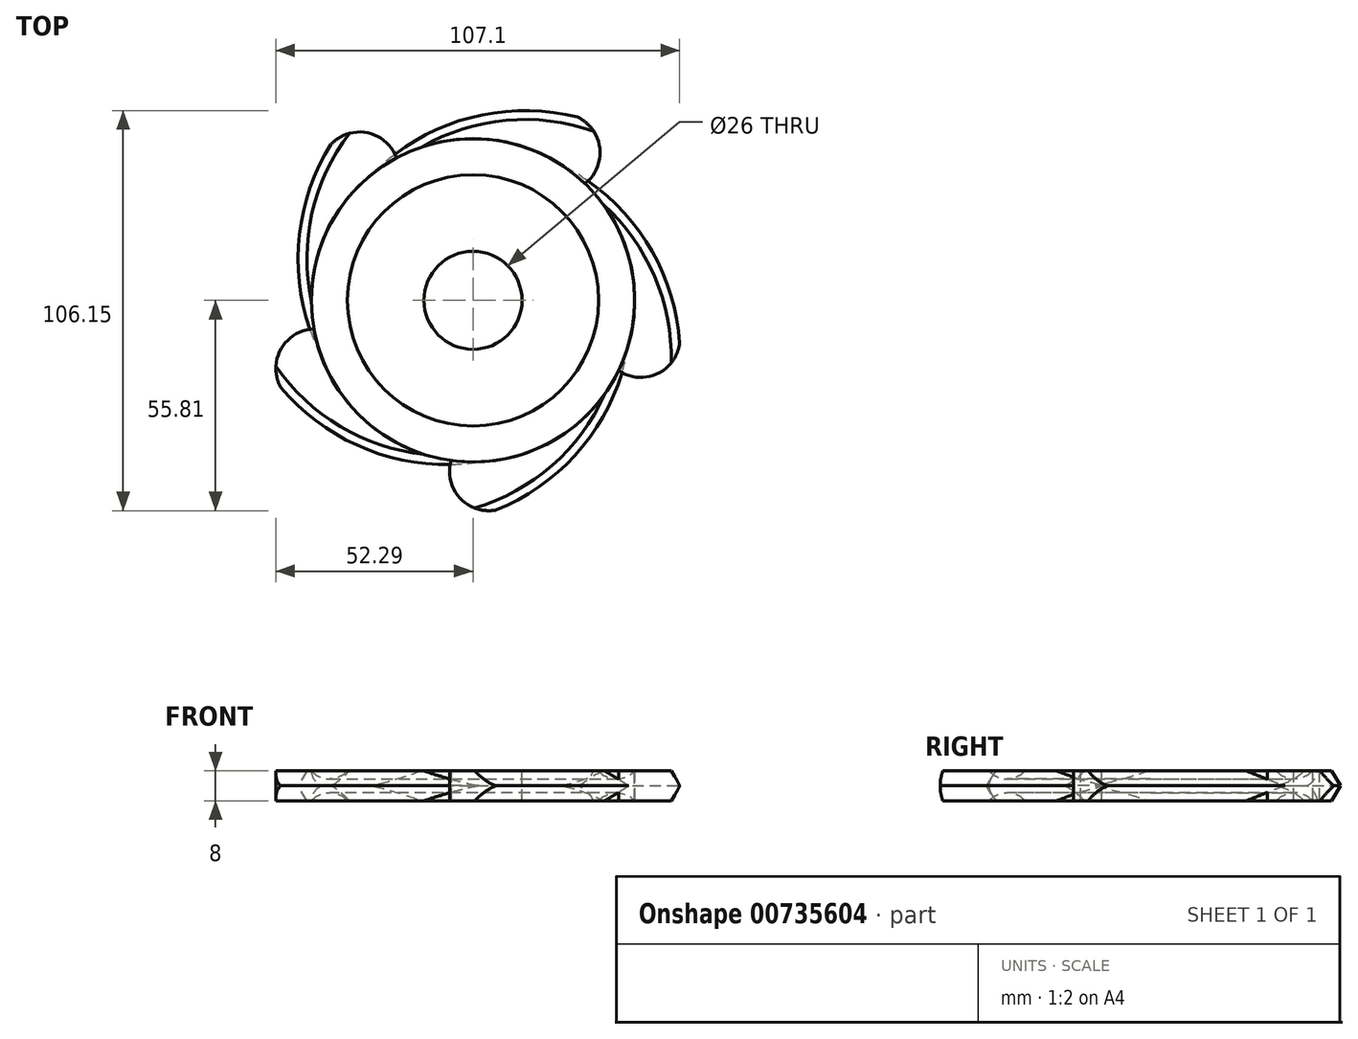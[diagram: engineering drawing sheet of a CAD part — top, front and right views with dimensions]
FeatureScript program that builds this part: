
annotation { "Feature Type Name" : "Feature", "Feature Type Description" : "" }
export const myFeature = defineFeature(function(context is Context, id is Id, definition is map)
    precondition{}
    {
        {
            var Q0;
            Q0=qCreatedBy(makeId("Front.planeOp"),FACE);
            var sketch = newSketch(context, id + "F0", { "sketchPlane" : qUnion([Q0])});
            skPoint(sketch, "E0", {"position": v(-13, 0) * mm});
            skLineSegment(sketch, "E1", {"start": v(-13, 0) * mm, "end": v(-13, 4) * mm});
            skLineSegment(sketch, "E2", {"start": v(0, 19.52) * mm, "end": v(0, -25.3) * mm});
            skLineSegment(sketch, "E3", {"start": v(-13, 4) * mm, "end": v(-33.32, 4) * mm});
            skArc(sketch, "E4", {"start": v(-42.9, 4) * mm, "mid": v(-38.1, 1.82) * mm, "end": v(-33.32, 4) * mm});
            skLineSegment(sketch, "E5", {"start": v(-42.9, 4) * mm, "end": v(-42.9, 0) * mm});
            skLineSegment(sketch, "E6", {"start": v(-42.9, 0) * mm, "end": v(-13, 0) * mm});
            skSolve(sketch);
        }
        {
            var Q0;
            Q0=makeQuery(id+"F0.imprint","IMPRINT",FACE,{"disambiguationData":[TD([[makeQuery(id+"F0.imprint","IMPRINT",EDGE,{"derivedFrom":sQuery(id+"F0.wireOp",EDGE,"E1")}),1.0]])]});
            var Q1;
            Q1=sQuery(id+"F0.wireOp",EDGE,"E2");
            revolve(context, id + "F1", {"surfaceOperationType" : NewSurfaceOperationType.NEW, "entities" : qUnion([Q0]), "axis" : qUnion([Q1]), "revolveType" : RevolveType.FULL});
        }
        {
            var Q0;
            Q0=qCreatedBy(makeId("Top.planeOp"),FACE);
            var sketch = newSketch(context, id + "F2", { "sketchPlane" : qUnion([Q0])});
            skArc(sketch, "E7", {"start": v(26.45, 49.12) * mm, "mid": v(-2.86, 48.06) * mm, "end": v(-27.82, 32.65) * mm});
            skCircle(sketch, "E8", {"center": v(0, 0) * mm, "radius": 42.9 * mm});
            skArc(sketch, "E9", {"start": v(29.69, 30.96) * mm, "mid": v(33.54, 41.02) * mm, "end": v(26.45, 49.12) * mm});
            skSolve(sketch);
        }
        {
            var Q0;
            Q0=makeQuery(id+"F1.opRevolve","SWEPT_BODY",BODY,{"disambiguationData":[OSD([sQuery(id+"F0.wireOp",EDGE,"E1"),sQuery(id+"F0.wireOp",EDGE,"E3"),sQuery(id+"F0.wireOp",EDGE,"E4"),sQuery(id+"F0.wireOp",EDGE,"E5"),sQuery(id+"F0.wireOp",EDGE,"E6")])]});
            var Q1;
            {var subQ0=sQuery(id+"F2.wireOp",EDGE,"E8");var subQ1=makeQuery(id+"F2.imprint","INTERSECT",VERTEX,{"derivedFrom":[sQuery(id+"F2.wireOp",EDGE,"E7"),subQ0]});Q1=makeQuery(id+"F2.imprint","IMPRINT",FACE,{"disambiguationData":[TD([[makeQuery(id+"F2.imprint","IMPRINT",EDGE,{"disambiguationData":[TD([[subQ1,1.0]])],"derivedFrom":subQ0}),1.0]])]});}
            mirror(context, id + "F3", {"operationType" : NewBodyOperationType.ADD, "entities" : qUnion([Q0]), "mirrorPlane" : qUnion([Q1])});
        }
        {
            var Q0;
            {var subQ0=sQuery(id+"F2.wireOp",EDGE,"E7");Q0=makeQuery(id+"F2.imprint","IMPRINT",FACE,{"disambiguationData":[TD([[makeQuery(id+"F2.imprint","IMPRINT",EDGE,{"derivedFrom":subQ0}),1.0]])]});}
            extrude(context, id + "F4", {"entities" : qUnion([Q0]), "endBound" : BoundingType.SYMMETRIC, "depth" : 8 * mm, "offsetDistance" : 25.4 * mm});
        }
        {
            var Q0;
            Q0=makeQuery(id+"F4.opExtrude","CAP_EDGE",EDGE,{"disambiguationData":[OSD([sQuery(id+"F2.wireOp",EDGE,"E7")])],"isStart":false});
            var Q1;
            Q1=makeQuery(id+"F4.opExtrude","CAP_EDGE",EDGE,{"disambiguationData":[OSD([sQuery(id+"F2.wireOp",EDGE,"E7")])],"isStart":true});
            chamfer(context, id + "F5", {"entities" : qUnion([Q0, Q1]), "chamferType" : ChamferType.TWO_OFFSETS, "width1" : 2.54 * mm, "oppositeDirection" : false, "width2" : 4.32 * mm, "tangentPropagation" : true});
        }
        {
            var Q0;
            Q0=makeQuery(id+"F4.opExtrude","SWEPT_BODY",BODY,{"disambiguationData":[OSD([sQuery(id+"F2.wireOp",EDGE,"E7"),sQuery(id+"F2.wireOp",EDGE,"E8"),sQuery(id+"F2.wireOp",EDGE,"E9")])]});
            var Q1;
            Q1=sQuery(id+"F0.wireOp",EDGE,"E2");
            circularPattern(context, id + "F6", {"entities" : qUnion([Q0]), "axis" : qUnion([Q1]), "angle" : 360 * degree, "instanceCount" : 5, "equalSpace" : true});
        }
    });
